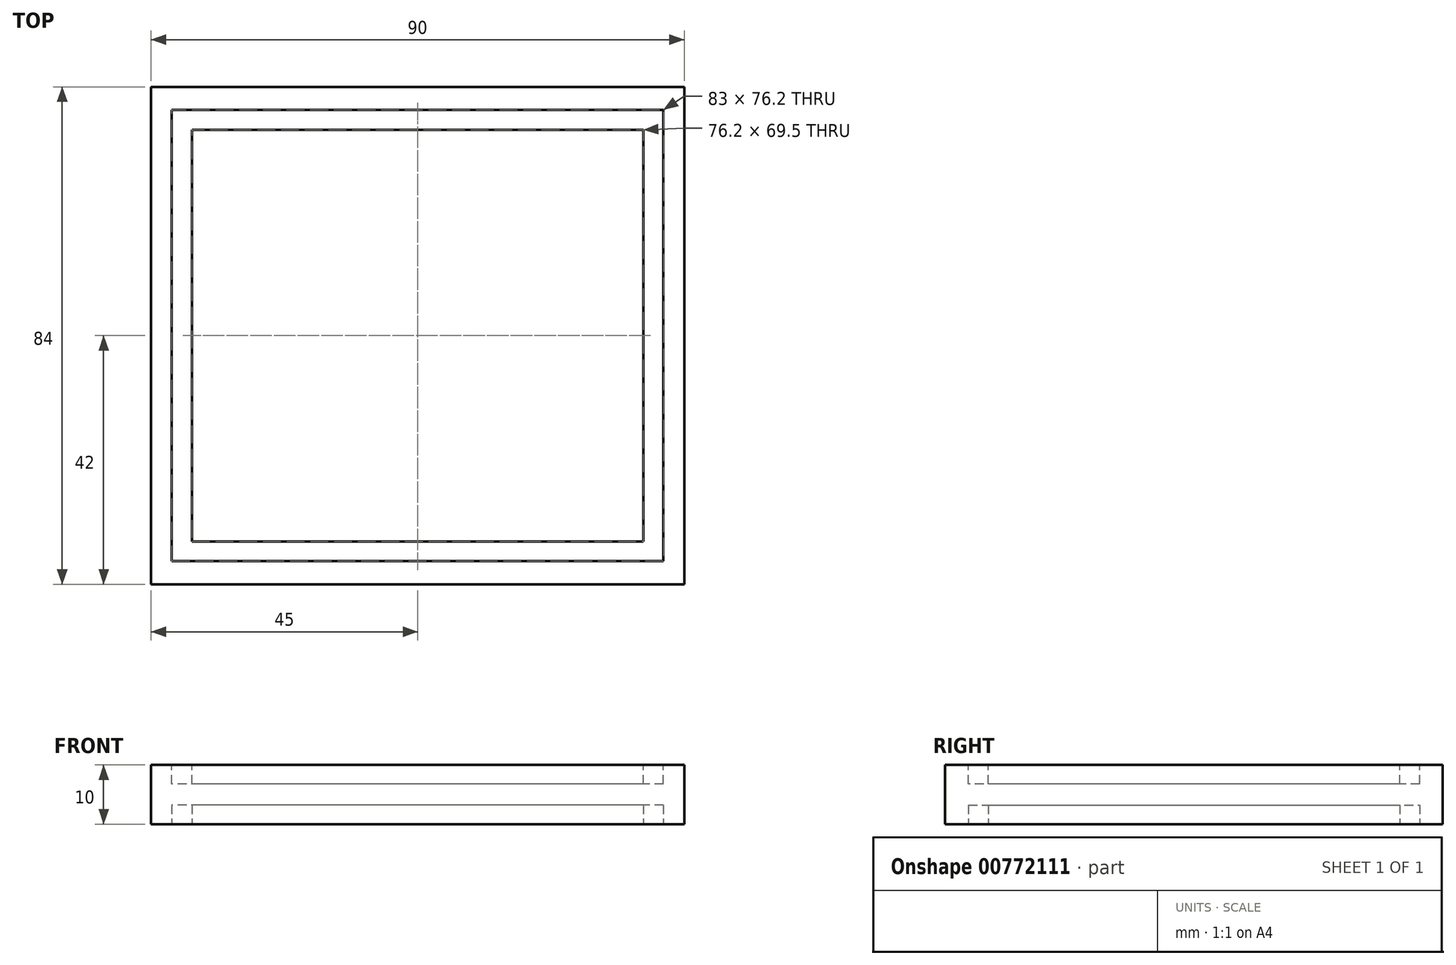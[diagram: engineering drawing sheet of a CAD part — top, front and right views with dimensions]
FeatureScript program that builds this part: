
annotation { "Feature Type Name" : "Feature", "Feature Type Description" : "" }
export const myFeature = defineFeature(function(context is Context, id is Id, definition is map)
    precondition{}
    {
        {
            var Q0;
            Q0=qCreatedBy(makeId("Top.planeOp"),FACE);
            var sketch = newSketch(context, id + "F0", { "sketchPlane" : qUnion([Q0])});
            skLineSegment(sketch, "E0.bottom", {"start": v(45, 42) * mm, "end": v(-45, 42) * mm});
            skLineSegment(sketch, "E0.top", {"start": v(45, -42) * mm, "end": v(-45, -42) * mm});
            skLineSegment(sketch, "E0.left", {"start": v(45, 42) * mm, "end": v(45, -42) * mm});
            skLineSegment(sketch, "E0.right", {"start": v(-45, 42) * mm, "end": v(-45, -42) * mm});
            skPoint(sketch, "E0.middle", {"position": v(0, 0) * mm});
            skSolve(sketch);
        }
        {
            var Q0;
            Q0=qSketchRegion(id+"F0",true);
            extrude(context, id + "F1", {"entities" : qUnion([Q0]), "depth" : 10 * mm, "offsetDistance" : 25 * mm});
        }
        {
            var Q0;
            Q0=makeQuery(id+"F1.opExtrude","CAP_FACE",FACE,{"disambiguationData":[OSD([sQuery(id+"F0.wireOp",EDGE,"E0.bottom"),sQuery(id+"F0.wireOp",EDGE,"E0.top"),sQuery(id+"F0.wireOp",EDGE,"E0.left"),sQuery(id+"F0.wireOp",EDGE,"E0.right")])],"isStart":false});
            var sketch = newSketch(context, id + "F2", { "sketchPlane" : qUnion([Q0])});
            skLineSegment(sketch, "E1.bottom", {"start": v(41.5, 38.1) * mm, "end": v(-41.5, 38.1) * mm});
            skLineSegment(sketch, "E1.top", {"start": v(41.5, -38.1) * mm, "end": v(-41.5, -38.1) * mm});
            skLineSegment(sketch, "E1.left", {"start": v(41.5, 38.1) * mm, "end": v(41.5, -38.1) * mm});
            skLineSegment(sketch, "E1.right", {"start": v(-41.5, 38.1) * mm, "end": v(-41.5, -38.1) * mm});
            skPoint(sketch, "E1.middle", {"position": v(0, 0) * mm});
            skLineSegment(sketch, "E2.bottom", {"start": v(38.1, 34.75) * mm, "end": v(-38.1, 34.75) * mm});
            skLineSegment(sketch, "E2.top", {"start": v(38.1, -34.75) * mm, "end": v(-38.1, -34.75) * mm});
            skLineSegment(sketch, "E2.left", {"start": v(38.1, 34.75) * mm, "end": v(38.1, -34.75) * mm});
            skLineSegment(sketch, "E2.right", {"start": v(-38.1, 34.75) * mm, "end": v(-38.1, -34.75) * mm});
            skSolve(sketch);
        }
        {
            var Q0;
            Q0=qSketchRegion(id+"F2",true);
            extrude(context, id + "F3", {"entities" : qUnion([Q0]), "operationType" : NewBodyOperationType.REMOVE, "oppositeDirection" : true, "depth" : 3.2 * mm, "offsetDistance" : 25 * mm});
        }
        {
            var Q0;
            Q0=makeQuery(id+"F1.opExtrude","CAP_FACE",FACE,{"disambiguationData":[OSD([sQuery(id+"F0.wireOp",EDGE,"E0.bottom"),sQuery(id+"F0.wireOp",EDGE,"E0.top"),sQuery(id+"F0.wireOp",EDGE,"E0.left"),sQuery(id+"F0.wireOp",EDGE,"E0.right")])],"isStart":true});
            var sketch = newSketch(context, id + "F4", { "sketchPlane" : qUnion([Q0])});
            skLineSegment(sketch, "E3.bottom", {"start": v(41.5, 38.1) * mm, "end": v(-41.5, 38.1) * mm});
            skLineSegment(sketch, "E3.top", {"start": v(41.5, -38.1) * mm, "end": v(-41.5, -38.1) * mm});
            skLineSegment(sketch, "E3.left", {"start": v(41.5, 38.1) * mm, "end": v(41.5, -38.1) * mm});
            skLineSegment(sketch, "E3.right", {"start": v(-41.5, 38.1) * mm, "end": v(-41.5, -38.1) * mm});
            skPoint(sketch, "E3.middle", {"position": v(0, 0) * mm});
            skLineSegment(sketch, "E4.bottom", {"start": v(38.1, 34.75) * mm, "end": v(-38.1, 34.75) * mm});
            skLineSegment(sketch, "E4.top", {"start": v(38.1, -34.75) * mm, "end": v(-38.1, -34.75) * mm});
            skLineSegment(sketch, "E4.left", {"start": v(38.1, 34.75) * mm, "end": v(38.1, -34.75) * mm});
            skLineSegment(sketch, "E4.right", {"start": v(-38.1, 34.75) * mm, "end": v(-38.1, -34.75) * mm});
            skSolve(sketch);
        }
        {
            var Q0;
            Q0 = qSketchRegion(id + "F4", true);
            extrude(context, id + "F5", {"entities" : qUnion([Q0]), "operationType" : NewBodyOperationType.REMOVE, "oppositeDirection" : true, "depth" : 3.2 * mm, "offsetDistance" : 25 * mm});
        }
    });
